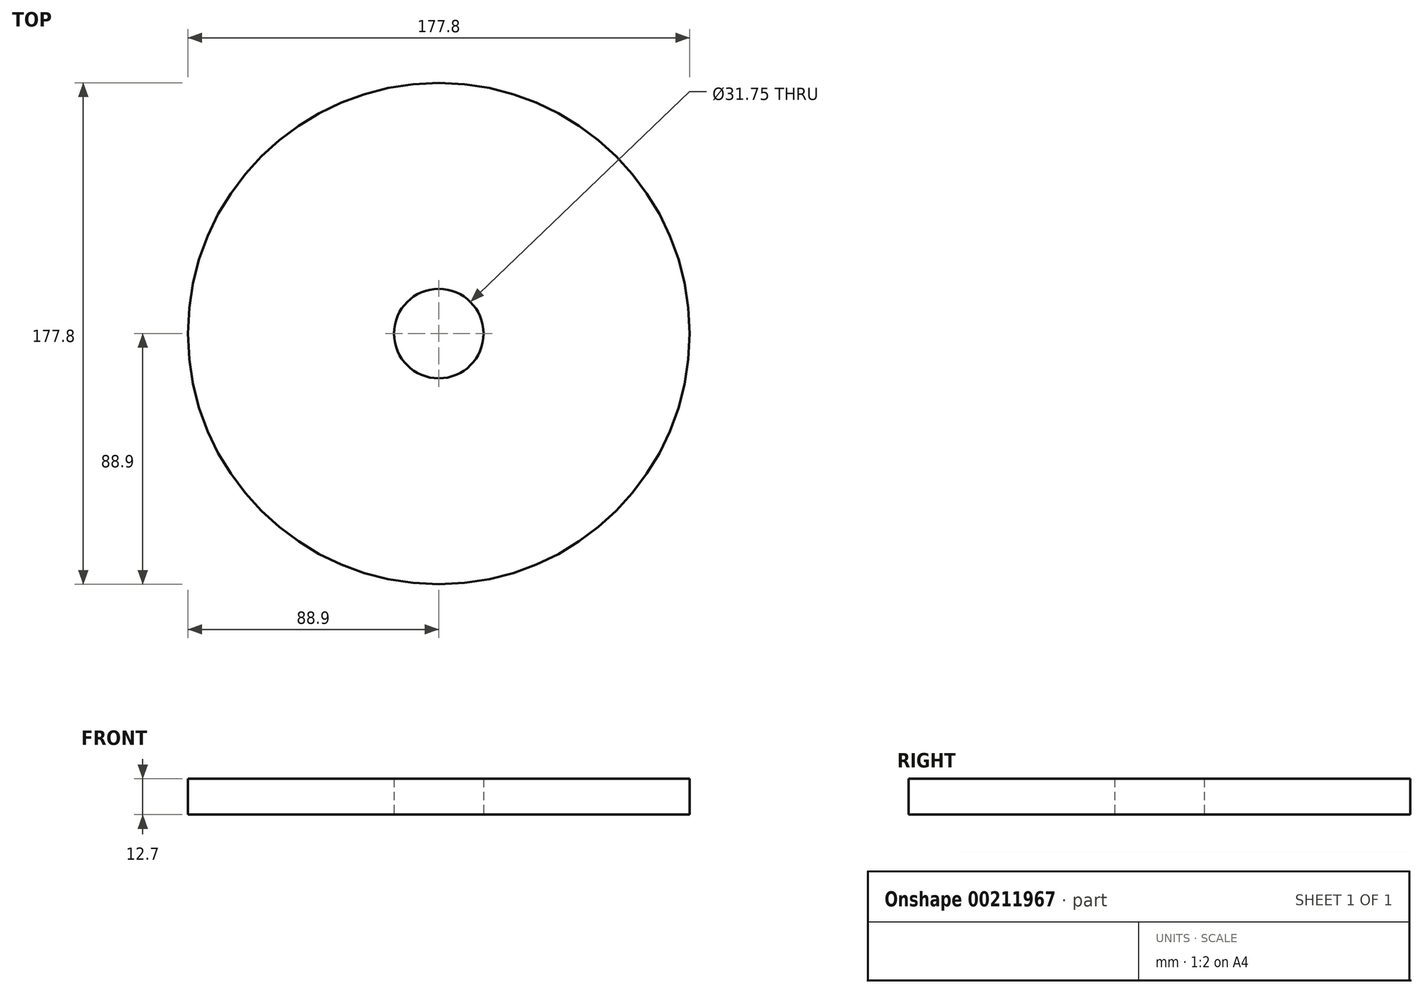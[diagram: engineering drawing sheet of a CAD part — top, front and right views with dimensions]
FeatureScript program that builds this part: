
annotation { "Feature Type Name" : "Feature", "Feature Type Description" : "" }
export const myFeature = defineFeature(function(context is Context, id is Id, definition is map)
    precondition{}
    {
        {
            var Q0;
            Q0=qCreatedBy(makeId("Top.planeOp"),FACE);
            var sketch = newSketch(context, id + "F0", { "sketchPlane" : qUnion([Q0])});
            skCircle(sketch, "E0", {"center": v(0, 0) * mm, "radius": 88.9 * mm});
            skCircle(sketch, "E1", {"center": v(0, 0) * mm, "radius": 15.88 * mm});
            skSolve(sketch);
        }
        {
            var Q0;
            Q0=makeQuery(id+"F0.imprint","IMPRINT",FACE,{"disambiguationData":[TD([[makeQuery(id+"F0.imprint","IMPRINT",EDGE,{"derivedFrom":sQuery(id+"F0.wireOp",EDGE,"E0")}),1.0]])]});
            extrude(context, id + "F1", {"entities" : qUnion([Q0]), "depth" : 12.7 * mm});
        }
    });
